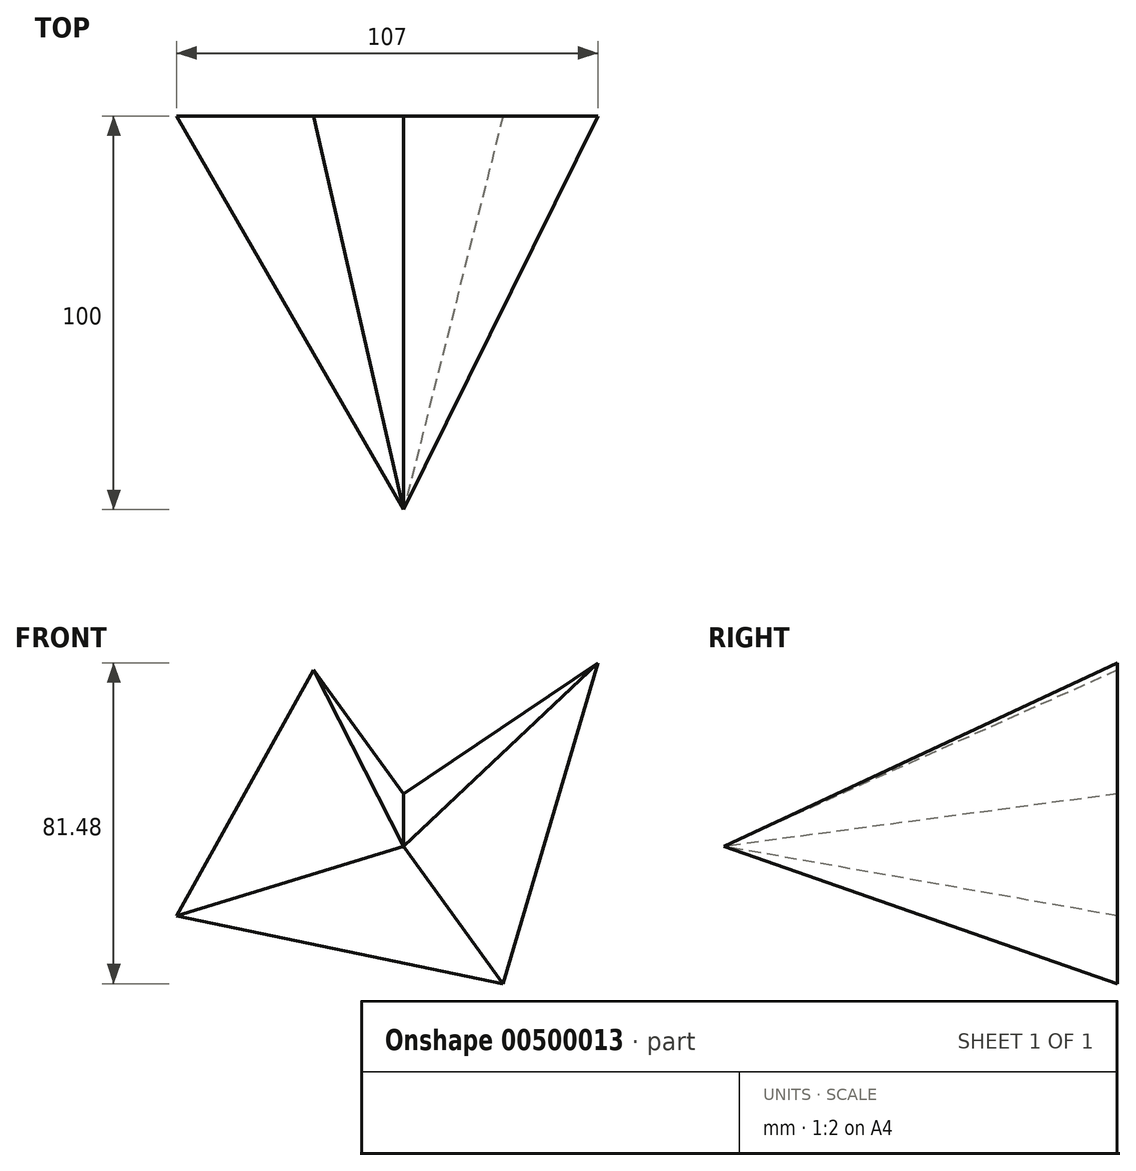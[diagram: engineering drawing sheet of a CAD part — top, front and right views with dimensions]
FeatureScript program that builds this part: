
annotation { "Feature Type Name" : "Feature", "Feature Type Description" : "" }
export const myFeature = defineFeature(function(context is Context, id is Id, definition is map)
    precondition{}
    {
        {
            var Q0;
            Q0=qCreatedBy(makeId("Front.planeOp"),FACE);
            var sketch = newSketch(context, id + "F0", { "sketchPlane" : qUnion([Q0])});
            skLineSegment(sketch, "E0", {"start": v(-22.66, 45.18) * mm, "end": v(-57.66, -17.64) * mm});
            skLineSegment(sketch, "E1", {"start": v(-22.95, 44.9) * mm, "end": v(0, 13.34) * mm});
            skLineSegment(sketch, "E2", {"start": v(0, 13.34) * mm, "end": v(49.34, 46.62) * mm});
            skLineSegment(sketch, "E3", {"start": v(49.34, 46.62) * mm, "end": v(25.25, -34.86) * mm});
            skLineSegment(sketch, "E4", {"start": v(25.25, -34.86) * mm, "end": v(-57.66, -17.64) * mm});
            skSolve(sketch);
        }
        {
            var Q0;
            Q0=qCreatedBy(makeId("Front.planeOp"),FACE);
            cPlane(context, id + "F1", {"entities" : qUnion([Q0]), "cplaneType" : CPlaneType.OFFSET, "offset" : 100 * mm, "width" : 150 * mm, "height" : 150 * mm});
        }
        {
            var Q0;
            Q0=qCreatedBy(id+"F1.planeOp",FACE);
            var sketch = newSketch(context, id + "F2", { "sketchPlane" : qUnion([Q0])});
            skPoint(sketch, "E5", {"position": v(0, 0) * mm});
            skSolve(sketch);
        }
        {
            var Q0;
            {var subQ0=sQuery(id+"F0.wireOp",EDGE,"E2");Q0=makeQuery(id+"F0.imprint","IMPRINT",FACE,{"disambiguationData":[TD([[makeQuery(id+"F0.imprint","IMPRINT",EDGE,{"derivedFrom":subQ0}),-1.0]])]});}
            var Q1;
            Q1=sQuery(id+"F2.wireOp",VERTEX,"E5");
            loft(context, id + "F3", {"sheetProfilesArray" : [{ "sheetProfileEntities" : qUnion([Q0]) }, { "sheetProfileEntities" : qUnion([Q1]) }]});
        }
    });
